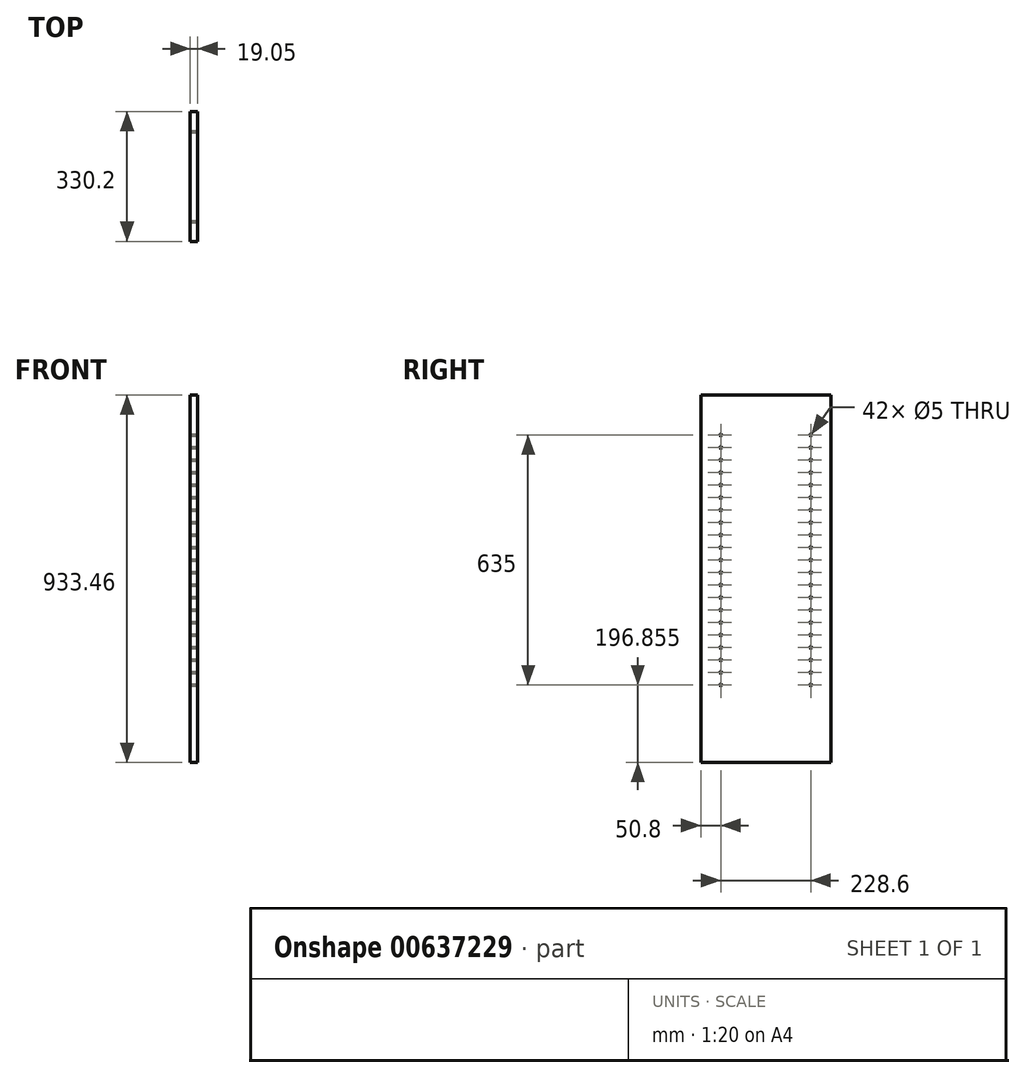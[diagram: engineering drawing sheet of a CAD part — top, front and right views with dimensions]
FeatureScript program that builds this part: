
annotation { "Feature Type Name" : "Feature", "Feature Type Description" : "" }
export const myFeature = defineFeature(function(context is Context, id is Id, definition is map)
    precondition{}
    {
        {
            var Q0;
            Q0=qCreatedBy(makeId("Right.planeOp"),FACE);
            var sketch = newSketch(context, id + "F0", { "sketchPlane" : qUnion([Q0])});
            skLineSegment(sketch, "E0.bottom", {"start": v(165.1, 466.73) * mm, "end": v(-165.1, 466.72) * mm});
            skLineSegment(sketch, "E0.top", {"start": v(165.1, -466.73) * mm, "end": v(-165.1, -466.73) * mm});
            skLineSegment(sketch, "E0.left", {"start": v(165.1, 466.72) * mm, "end": v(165.1, -466.73) * mm});
            skLineSegment(sketch, "E0.right", {"start": v(-165.1, 466.72) * mm, "end": v(-165.1, -466.73) * mm});
            skPoint(sketch, "E0.middle", {"position": v(0, 0) * mm});
            skSolve(sketch);
        }
        {
            var Q0;
            Q0=makeQuery(id+"F0.imprint","IMPRINT",FACE,{"disambiguationData":[TD([[makeQuery(id+"F0.imprint","IMPRINT",EDGE,{"derivedFrom":sQuery(id+"F0.wireOp",EDGE,"E0.bottom")}),1.0]])]});
            extrude(context, id + "F1", {"entities" : qUnion([Q0]), "depth" : 19.05 * mm, "offsetDistance" : 25.4 * mm});
        }
        {
            var Q0;
            Q0=makeQuery(id+"F1.opExtrude","CAP_FACE",FACE,{"disambiguationData":[OSD([sQuery(id+"F0.wireOp",EDGE,"E0.bottom"),sQuery(id+"F0.wireOp",EDGE,"E0.top"),sQuery(id+"F0.wireOp",EDGE,"E0.left"),sQuery(id+"F0.wireOp",EDGE,"E0.right")])],"isStart":false});
            var sketch = newSketch(context, id + "F2", { "sketchPlane" : qUnion([Q0])});
            skLineSegment(sketch, "E1", {"start": v(0, 466.72) * mm, "end": v(0, 333.37) * mm});
            skLineSegment(sketch, "E2.bottom", {"start": v(114.3, 301.62) * mm, "end": v(-114.3, 301.62) * mm});
            skLineSegment(sketch, "E2.top", {"start": v(114.3, 365.12) * mm, "end": v(-114.3, 365.12) * mm});
            skLineSegment(sketch, "E2.left", {"start": v(114.3, 301.62) * mm, "end": v(114.3, 365.12) * mm});
            skLineSegment(sketch, "E2.right", {"start": v(-114.3, 301.62) * mm, "end": v(-114.3, 365.12) * mm});
            skPoint(sketch, "E2.middle", {"position": v(0, 333.37) * mm});
            skLineSegment(sketch, "E3", {"start": v(0, 301.62) * mm, "end": v(0, 238.12) * mm});
            skLineSegment(sketch, "E4.bottom", {"start": v(-114.3, 206.37) * mm, "end": v(114.3, 206.37) * mm});
            skLineSegment(sketch, "E4.top", {"start": v(-114.3, 269.88) * mm, "end": v(114.3, 269.88) * mm});
            skLineSegment(sketch, "E4.left", {"start": v(-114.3, 206.37) * mm, "end": v(-114.3, 269.88) * mm});
            skLineSegment(sketch, "E4.right", {"start": v(114.3, 206.37) * mm, "end": v(114.3, 269.88) * mm});
            skPoint(sketch, "E4.middle", {"position": v(0, 238.12) * mm});
            skLineSegment(sketch, "E5", {"start": v(0, 206.37) * mm, "end": v(0, 142.87) * mm});
            skLineSegment(sketch, "E6.bottom", {"start": v(-114.3, 174.63) * mm, "end": v(114.3, 174.63) * mm});
            skLineSegment(sketch, "E6.top", {"start": v(-114.3, 111.13) * mm, "end": v(114.3, 111.13) * mm});
            skLineSegment(sketch, "E6.left", {"start": v(-114.3, 174.63) * mm, "end": v(-114.3, 111.13) * mm});
            skLineSegment(sketch, "E6.right", {"start": v(114.3, 174.63) * mm, "end": v(114.3, 111.13) * mm});
            skPoint(sketch, "E6.middle", {"position": v(0, 142.87) * mm});
            skLineSegment(sketch, "E7", {"start": v(0, 111.13) * mm, "end": v(0, 47.63) * mm});
            skPoint(sketch, "E7.endSnap0", {"position": v(0, 111.13) * mm});
            skLineSegment(sketch, "E8.bottom", {"start": v(-114.3, 79.38) * mm, "end": v(114.3, 79.38) * mm});
            skLineSegment(sketch, "E8.top", {"start": v(-114.3, 15.88) * mm, "end": v(114.3, 15.88) * mm});
            skLineSegment(sketch, "E8.left", {"start": v(-114.3, 79.38) * mm, "end": v(-114.3, 15.88) * mm});
            skLineSegment(sketch, "E8.right", {"start": v(114.3, 79.38) * mm, "end": v(114.3, 15.88) * mm});
            skPoint(sketch, "E8.middle", {"position": v(0, 47.63) * mm});
            skLineSegment(sketch, "E9", {"start": v(0, 15.88) * mm, "end": v(0, -47.62) * mm});
            skLineSegment(sketch, "E10.bottom", {"start": v(-114.3, -15.87) * mm, "end": v(114.3, -15.87) * mm});
            skLineSegment(sketch, "E10.top", {"start": v(-114.3, -79.37) * mm, "end": v(114.3, -79.37) * mm});
            skLineSegment(sketch, "E10.left", {"start": v(-114.3, -15.87) * mm, "end": v(-114.3, -79.37) * mm});
            skLineSegment(sketch, "E10.right", {"start": v(114.3, -15.87) * mm, "end": v(114.3, -79.37) * mm});
            skPoint(sketch, "E10.middle", {"position": v(0, -47.62) * mm});
            skLineSegment(sketch, "E11", {"start": v(0, -79.37) * mm, "end": v(0, -142.87) * mm});
            skLineSegment(sketch, "E12.bottom", {"start": v(-114.3, -111.12) * mm, "end": v(114.3, -111.12) * mm});
            skLineSegment(sketch, "E12.top", {"start": v(-114.3, -174.62) * mm, "end": v(114.3, -174.62) * mm});
            skLineSegment(sketch, "E12.left", {"start": v(-114.3, -111.12) * mm, "end": v(-114.3, -174.62) * mm});
            skLineSegment(sketch, "E12.right", {"start": v(114.3, -111.12) * mm, "end": v(114.3, -174.62) * mm});
            skPoint(sketch, "E12.middle", {"position": v(0, -142.87) * mm});
            skLineSegment(sketch, "E13", {"start": v(0, -174.62) * mm, "end": v(0, -238.12) * mm});
            skLineSegment(sketch, "E14.bottom", {"start": v(-114.3, -206.37) * mm, "end": v(114.3, -206.37) * mm});
            skLineSegment(sketch, "E14.top", {"start": v(-114.3, -269.88) * mm, "end": v(114.3, -269.88) * mm});
            skLineSegment(sketch, "E14.left", {"start": v(-114.3, -206.37) * mm, "end": v(-114.3, -269.88) * mm});
            skLineSegment(sketch, "E14.right", {"start": v(114.3, -206.37) * mm, "end": v(114.3, -269.88) * mm});
            skPoint(sketch, "E14.middle", {"position": v(0, -238.12) * mm});
            skPoint(sketch, "E15", {"position": v(114.3, 365.12) * mm});
            skPoint(sketch, "E16", {"position": v(114.3, 333.37) * mm});
            skPoint(sketch, "E17", {"position": v(114.3, 301.62) * mm});
            skPoint(sketch, "E18", {"position": v(114.3, 269.88) * mm});
            skPoint(sketch, "E19", {"position": v(114.3, 238.12) * mm});
            skPoint(sketch, "E20", {"position": v(114.3, 206.37) * mm});
            skPoint(sketch, "E21", {"position": v(114.3, 174.63) * mm});
            skPoint(sketch, "E22", {"position": v(114.3, 142.88) * mm});
            skPoint(sketch, "E23", {"position": v(114.3, 111.13) * mm});
            skPoint(sketch, "E24", {"position": v(114.3, 79.38) * mm});
            skPoint(sketch, "E25", {"position": v(114.3, 47.63) * mm});
            skPoint(sketch, "E26", {"position": v(114.3, 15.88) * mm});
            skPoint(sketch, "E27", {"position": v(114.3, -15.87) * mm});
            skPoint(sketch, "E28", {"position": v(114.3, -47.62) * mm});
            skPoint(sketch, "E29", {"position": v(114.3, -79.37) * mm});
            skPoint(sketch, "E30", {"position": v(114.3, -111.12) * mm});
            skPoint(sketch, "E31", {"position": v(114.3, -142.87) * mm});
            skPoint(sketch, "E32", {"position": v(114.3, -174.62) * mm});
            skPoint(sketch, "E33", {"position": v(114.3, -206.37) * mm});
            skPoint(sketch, "E34", {"position": v(114.3, -238.12) * mm});
            skPoint(sketch, "E35", {"position": v(114.3, -269.88) * mm});
            skPoint(sketch, "E36", {"position": v(-114.3, -269.88) * mm});
            skPoint(sketch, "E37", {"position": v(-114.3, -238.12) * mm});
            skPoint(sketch, "E38", {"position": v(-114.3, -206.37) * mm});
            skPoint(sketch, "E39", {"position": v(-114.3, -174.62) * mm});
            skPoint(sketch, "E40", {"position": v(-114.3, -142.87) * mm});
            skPoint(sketch, "E41", {"position": v(-114.3, -111.12) * mm});
            skPoint(sketch, "E42", {"position": v(-114.3, -79.37) * mm});
            skPoint(sketch, "E43", {"position": v(-114.3, -47.62) * mm});
            skPoint(sketch, "E44", {"position": v(-114.3, -15.87) * mm});
            skPoint(sketch, "E45", {"position": v(-114.3, 15.88) * mm});
            skPoint(sketch, "E46", {"position": v(-114.3, 47.63) * mm});
            skPoint(sketch, "E47", {"position": v(-114.3, 79.38) * mm});
            skPoint(sketch, "E48", {"position": v(-114.3, 111.13) * mm});
            skPoint(sketch, "E49", {"position": v(-114.3, 142.88) * mm});
            skPoint(sketch, "E50", {"position": v(-114.3, 174.63) * mm});
            skPoint(sketch, "E51", {"position": v(-114.3, 206.37) * mm});
            skPoint(sketch, "E52", {"position": v(-114.3, 238.12) * mm});
            skPoint(sketch, "E53", {"position": v(-114.3, 269.88) * mm});
            skPoint(sketch, "E54", {"position": v(-114.3, 301.62) * mm});
            skPoint(sketch, "E55", {"position": v(-114.3, 333.37) * mm});
            skPoint(sketch, "E56", {"position": v(-114.3, 365.12) * mm});
            skSolve(sketch);
        }
        {
            var Q0;
            Q0=sQuery(id+"F2.wireOp",VERTEX,"E56");
            var Q1;
            Q1=sQuery(id+"F2.wireOp",VERTEX,"E55");
            var Q2;
            Q2=sQuery(id+"F2.wireOp",VERTEX,"E54");
            var Q3;
            Q3=sQuery(id+"F2.wireOp",VERTEX,"E53");
            var Q4;
            Q4=sQuery(id+"F2.wireOp",VERTEX,"E52");
            var Q5;
            Q5=sQuery(id+"F2.wireOp",VERTEX,"E51");
            var Q6;
            Q6=sQuery(id+"F2.wireOp",VERTEX,"E50");
            var Q7;
            Q7=sQuery(id+"F2.wireOp",VERTEX,"E49");
            var Q8;
            Q8=sQuery(id+"F2.wireOp",VERTEX,"E48");
            var Q9;
            Q9=sQuery(id+"F2.wireOp",VERTEX,"E47");
            var Q10;
            Q10=sQuery(id+"F2.wireOp",VERTEX,"E46");
            var Q11;
            Q11=sQuery(id+"F2.wireOp",VERTEX,"E45");
            var Q12;
            Q12=sQuery(id+"F2.wireOp",VERTEX,"E44");
            var Q13;
            Q13=sQuery(id+"F2.wireOp",VERTEX,"E42");
            var Q14;
            Q14=sQuery(id+"F2.wireOp",VERTEX,"E43");
            var Q15;
            Q15=sQuery(id+"F2.wireOp",VERTEX,"E41");
            var Q16;
            Q16=sQuery(id+"F2.wireOp",VERTEX,"E39");
            var Q17;
            Q17=sQuery(id+"F2.wireOp",VERTEX,"E40");
            var Q18;
            Q18=sQuery(id+"F2.wireOp",VERTEX,"E38");
            var Q19;
            Q19=sQuery(id+"F2.wireOp",VERTEX,"E37");
            var Q20;
            Q20=sQuery(id+"F2.wireOp",VERTEX,"E36");
            var Q21;
            Q21=sQuery(id+"F2.wireOp",VERTEX,"E35");
            var Q22;
            Q22=sQuery(id+"F2.wireOp",VERTEX,"E34");
            var Q23;
            Q23=sQuery(id+"F2.wireOp",VERTEX,"E33");
            var Q24;
            Q24=sQuery(id+"F2.wireOp",VERTEX,"E32");
            var Q25;
            Q25=sQuery(id+"F2.wireOp",VERTEX,"E31");
            var Q26;
            Q26=sQuery(id+"F2.wireOp",VERTEX,"E30");
            var Q27;
            Q27=sQuery(id+"F2.wireOp",VERTEX,"E29");
            var Q28;
            Q28=sQuery(id+"F2.wireOp",VERTEX,"E28");
            var Q29;
            Q29=sQuery(id+"F2.wireOp",VERTEX,"E27");
            var Q30;
            Q30=sQuery(id+"F2.wireOp",VERTEX,"E26");
            var Q31;
            Q31=sQuery(id+"F2.wireOp",VERTEX,"E25");
            var Q32;
            Q32=sQuery(id+"F2.wireOp",VERTEX,"E24");
            var Q33;
            Q33=sQuery(id+"F2.wireOp",VERTEX,"E23");
            var Q34;
            Q34=sQuery(id+"F2.wireOp",VERTEX,"E22");
            var Q35;
            Q35=sQuery(id+"F2.wireOp",VERTEX,"E21");
            var Q36;
            Q36=sQuery(id+"F2.wireOp",VERTEX,"E20");
            var Q37;
            Q37=sQuery(id+"F2.wireOp",VERTEX,"E19");
            var Q38;
            Q38=sQuery(id+"F2.wireOp",VERTEX,"E18");
            var Q39;
            Q39=sQuery(id+"F2.wireOp",VERTEX,"E17");
            var Q40;
            Q40=sQuery(id+"F2.wireOp",VERTEX,"E16");
            var Q41;
            Q41=sQuery(id+"F2.wireOp",VERTEX,"E15");
            var Q42;
            Q42=sQuery(id+"F2.wireOp",VERTEX,"E23");
            var Q43;
            Q43=makeQuery(id+"F1.opExtrude","SWEPT_BODY",BODY,{"disambiguationData":[OSD([sQuery(id+"F0.wireOp",EDGE,"E0.bottom"),sQuery(id+"F0.wireOp",EDGE,"E0.top"),sQuery(id+"F0.wireOp",EDGE,"E0.left"),sQuery(id+"F0.wireOp",EDGE,"E0.right")])]});
            hole(context, id + "F3", {"style" : HoleStyle.SIMPLE, "endStyle" : HoleEndStyle.BLIND, "holeDiameter" : 5 * mm, "majorDiameter" : 6.35 * mm, "holeDepth" : 14.22 * mm, "isTappedThrough" : true, "tappedDepth" : 12.7 * mm, "tapClearance" : 3, "startFromSketch" : true, "locations" : qUnion([Q0, Q1, Q2, Q3, Q4, Q5, Q6, Q7, Q8, Q9, Q10, Q11, Q12, Q13, Q14, Q15, Q16, Q17, Q18, Q19, Q20, Q21, Q22, Q23, Q24, Q25, Q26, Q27, Q28, Q29, Q30, Q31, Q32, Q33, Q34, Q35, Q36, Q37, Q38, Q39, Q40, Q41, Q42]), "scope" : qUnion([Q43])});
        }
    });
